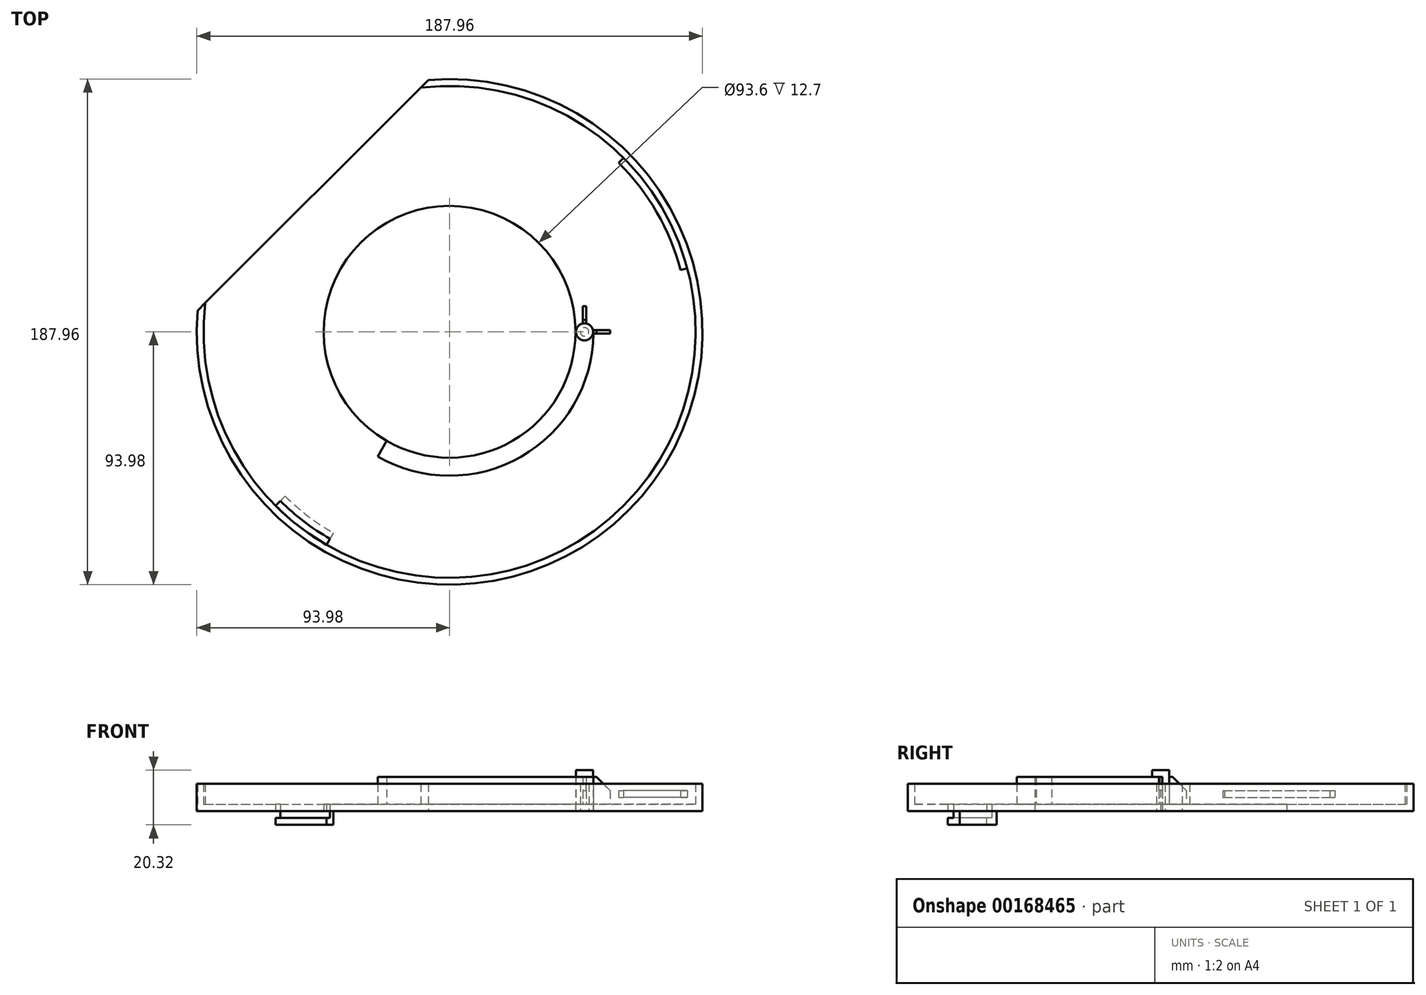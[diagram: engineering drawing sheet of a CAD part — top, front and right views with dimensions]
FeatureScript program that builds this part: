
annotation { "Feature Type Name" : "Feature", "Feature Type Description" : "" }
export const myFeature = defineFeature(function(context is Context, id is Id, definition is map)
    precondition{}
    {
        {
            var Q0;
            Q0=qCreatedBy(makeId("Top.planeOp"),FACE);
            var sketch = newSketch(context, id + "F0", { "sketchPlane" : qUnion([Q0])});
            skCircle(sketch, "E0", {"center": v(0, 0) * mm, "radius": 93.98 * mm});
            skCircle(sketch, "E1", {"center": v(0, 0) * mm, "radius": 46.8 * mm});
            skLineSegment(sketch, "E2", {"start": v(0, 92.98) * mm, "end": v(0, -89.42) * mm, "construction": true});
            skCircle(sketch, "E3", {"center": v(50.15, 0) * mm, "radius": 1.59 * mm});
            skCircle(sketch, "E4", {"center": v(50.15, 0) * mm, "radius": 3.18 * mm});
            skCircle(sketch, "E5", {"center": v(0, 0) * mm, "radius": 91.44 * mm});
            skLineSegment(sketch, "E6", {"start": v(0, 0) * mm, "end": v(-90.78, 24.32) * mm});
            skLineSegment(sketch, "E7", {"start": v(0, 0) * mm, "end": v(-66.45, 66.45) * mm});
            skCircle(sketch, "E8", {"center": v(0, 0) * mm, "radius": 88.9 * mm});
            skLineSegment(sketch, "E9.MirrorCS", {"start": v(0, 0) * mm, "end": v(66.45, 66.45) * mm});
            skLineSegment(sketch, "E10.MirrorCS", {"start": v(0, 0) * mm, "end": v(90.78, 24.32) * mm});
            skCircle(sketch, "E11", {"center": v(0, 0) * mm, "radius": 53.5 * mm});
            skPoint(sketch, "E12", {"position": v(46.8, 0) * mm});
            skPoint(sketch, "E13", {"position": v(53.5, 0) * mm});
            skLineSegment(sketch, "E14", {"start": v(46.8, 0) * mm, "end": v(53.5, 0) * mm});
            skLineSegment(sketch, "E15", {"start": v(0, 0) * mm, "end": v(103.4, 0) * mm, "construction": true});
            skLineSegment(sketch, "E16", {"start": v(49.52, 9.53) * mm, "end": v(49.52, -9.53) * mm});
            skLineSegment(sketch, "E17", {"start": v(50.78, 9.53) * mm, "end": v(50.78, -9.53) * mm});
            skLineSegment(sketch, "E18", {"start": v(50.78, -9.53) * mm, "end": v(49.52, -9.53) * mm});
            skLineSegment(sketch, "E19", {"start": v(50.78, 9.53) * mm, "end": v(49.52, 9.53) * mm});
            skPoint(sketch, "E20", {"position": v(49.52, 0) * mm});
            skLineSegment(sketch, "E21", {"start": v(50.15, 12) * mm, "end": v(50.15, -10.12) * mm, "construction": true});
            skPoint(sketch, "E22", {"position": v(50.15, 9.53) * mm});
            skLineSegment(sketch, "E23", {"start": v(50.15, 0.64) * mm, "end": v(59.67, 0.64) * mm});
            skLineSegment(sketch, "E24", {"start": v(59.67, -0.64) * mm, "end": v(59.67, 0.64) * mm});
            skLineSegment(sketch, "E25", {"start": v(50.15, -0.64) * mm, "end": v(59.67, -0.64) * mm});
            skPoint(sketch, "E26", {"position": v(59.67, 0) * mm});
            skLineSegment(sketch, "E27", {"start": v(0, 0) * mm, "end": v(-81.39, -47) * mm});
            skCircle(sketch, "E28", {"center": v(0, 0) * mm, "radius": 86.36 * mm});
            skLineSegment(sketch, "E29", {"start": v(0, 0) * mm, "end": v(-66.45, -66.45) * mm});
            skLineSegment(sketch, "E30", {"start": v(0, 0) * mm, "end": v(-46.99, -81.39) * mm});
            skLineSegment(sketch, "E31", {"start": v(-91.19, 6.77) * mm, "end": v(-6.77, 91.19) * mm});
            skLineSegment(sketch, "E32", {"start": v(-91.19, 6.77) * mm, "end": v(-93.9, 4.07) * mm});
            skLineSegment(sketch, "E33", {"start": v(-6.77, 91.19) * mm, "end": v(-4.07, 93.9) * mm});
            skLineSegment(sketch, "E34", {"start": v(-93.65, 7.9) * mm, "end": v(-7.9, 93.65) * mm});
            skSolve(sketch);
        }
        {
            var Q0;
            {var subQ0=sQuery(id+"F0.wireOp",EDGE,"E16");var subQ1=sQuery(id+"F0.wireOp",EDGE,"E3");var subQ2=makeQuery(id+"F0.imprint","INTERSECT",VERTEX,{"disambiguationData":[OD(0.0)],"derivedFrom":[subQ1,subQ0]});Q0=makeQuery(id+"F0.imprint","IMPRINT",FACE,{"disambiguationData":[TD([[makeQuery(id+"F0.imprint","IMPRINT",EDGE,{"disambiguationData":[TD([[subQ2,-1.0]])],"derivedFrom":subQ1}),-1.0]])]});}
            var Q1;
            {var subQ0=sQuery(id+"F0.wireOp",EDGE,"E25");var subQ1=sQuery(id+"F0.wireOp",EDGE,"E4");var subQ2=makeQuery(id+"F0.imprint","INTERSECT",VERTEX,{"derivedFrom":[subQ1,subQ0]});Q1=makeQuery(id+"F0.imprint","IMPRINT",FACE,{"disambiguationData":[TD([[makeQuery(id+"F0.imprint","IMPRINT",EDGE,{"disambiguationData":[TD([[subQ2,-1.0]])],"derivedFrom":subQ1}),-1.0]])]});}
            var Q2;
            {var subQ5=sQuery(id+"F0.wireOp",EDGE,"E11");var subQ6=sQuery(id+"F0.wireOp",EDGE,"E7");var subQ7=makeQuery(id+"F0.imprint","INTERSECT",VERTEX,{"derivedFrom":[subQ6,subQ5]});Q2=makeQuery(id+"F0.imprint","IMPRINT",FACE,{"disambiguationData":[TD([[makeQuery(id+"F0.imprint","IMPRINT",EDGE,{"disambiguationData":[TD([[subQ7,-1.0]])],"derivedFrom":subQ6}),-1.0]])]});}
            var Q3;
            {var subQ0=sQuery(id+"F0.wireOp",EDGE,"E17");var subQ1=sQuery(id+"F0.wireOp",EDGE,"E4");var subQ2=makeQuery(id+"F0.imprint","INTERSECT",VERTEX,{"disambiguationData":[OD(0.0)],"derivedFrom":[subQ1,subQ0]});Q3=makeQuery(id+"F0.imprint","IMPRINT",FACE,{"disambiguationData":[TD([[makeQuery(id+"F0.imprint","IMPRINT",EDGE,{"disambiguationData":[TD([[subQ2,1.0]])],"derivedFrom":subQ1}),1.0]])]});}
            var Q4;
            {var subQ0=sQuery(id+"F0.wireOp",EDGE,"E24");Q4=makeQuery(id+"F0.imprint","IMPRINT",FACE,{"disambiguationData":[TD([[makeQuery(id+"F0.imprint","IMPRINT",EDGE,{"derivedFrom":subQ0}),1.0]])]});}
            var Q5;
            {var subQ0=sQuery(id+"F0.wireOp",EDGE,"E17");var subQ1=sQuery(id+"F0.wireOp",EDGE,"E4");var subQ2=makeQuery(id+"F0.imprint","INTERSECT",VERTEX,{"disambiguationData":[OD(1.0)],"derivedFrom":[subQ1,subQ0]});Q5=makeQuery(id+"F0.imprint","IMPRINT",FACE,{"disambiguationData":[TD([[makeQuery(id+"F0.imprint","IMPRINT",EDGE,{"disambiguationData":[TD([[subQ2,-1.0]])],"derivedFrom":subQ1}),1.0]])]});}
            var Q6;
            {var subQ0=sQuery(id+"F0.wireOp",EDGE,"E9.MirrorCS");var subQ1=sQuery(id+"F0.wireOp",EDGE,"E0");var subQ2=makeQuery(id+"F0.imprint","INTERSECT",VERTEX,{"derivedFrom":[subQ1,subQ0]});Q6=makeQuery(id+"F0.imprint","IMPRINT",FACE,{"disambiguationData":[TD([[makeQuery(id+"F0.imprint","IMPRINT",EDGE,{"disambiguationData":[TD([[subQ2,1.0]])],"derivedFrom":subQ1}),1.0]])]});}
            var Q7;
            {var subQ0=sQuery(id+"F0.wireOp",EDGE,"E14");var subQ1=sQuery(id+"F0.wireOp",EDGE,"E4");var subQ2=makeQuery(id+"F0.imprint","INTERSECT",VERTEX,{"disambiguationData":[OD(1.0)],"derivedFrom":[subQ1,subQ0]});Q7=makeQuery(id+"F0.imprint","IMPRINT",FACE,{"disambiguationData":[TD([[makeQuery(id+"F0.imprint","IMPRINT",EDGE,{"disambiguationData":[TD([[subQ2,-1.0]])],"derivedFrom":subQ1}),-1.0]])]});}
            var Q8;
            {var subQ3=sQuery(id+"F0.wireOp",EDGE,"E9.MirrorCS");var subQ5=sQuery(id+"F0.wireOp",EDGE,"E8");var subQ6=makeQuery(id+"F0.imprint","INTERSECT",VERTEX,{"derivedFrom":[subQ5,subQ3]});Q8=makeQuery(id+"F0.imprint","IMPRINT",FACE,{"disambiguationData":[TD([[makeQuery(id+"F0.imprint","IMPRINT",EDGE,{"disambiguationData":[TD([[subQ6,-1.0]])],"derivedFrom":subQ5}),-1.0]])]});}
            var Q9;
            {var subQ0=sQuery(id+"F0.wireOp",EDGE,"E9.MirrorCS");var subQ1=sQuery(id+"F0.wireOp",EDGE,"E1");var subQ2=makeQuery(id+"F0.imprint","INTERSECT",VERTEX,{"derivedFrom":[subQ1,subQ0]});Q9=makeQuery(id+"F0.imprint","IMPRINT",FACE,{"disambiguationData":[TD([[makeQuery(id+"F0.imprint","IMPRINT",EDGE,{"disambiguationData":[TD([[subQ2,-1.0]])],"derivedFrom":subQ1}),-1.0]])]});}
            var Q10;
            {var subQ0=sQuery(id+"F0.wireOp",EDGE,"E10.MirrorCS");var subQ1=sQuery(id+"F0.wireOp",EDGE,"E1");var subQ2=makeQuery(id+"F0.imprint","INTERSECT",VERTEX,{"derivedFrom":[subQ1,subQ0]});Q10=makeQuery(id+"F0.imprint","IMPRINT",FACE,{"disambiguationData":[TD([[makeQuery(id+"F0.imprint","IMPRINT",EDGE,{"disambiguationData":[TD([[subQ2,-1.0]])],"derivedFrom":subQ1}),-1.0]])]});}
            var Q11;
            {var subQ5=sQuery(id+"F0.wireOp",EDGE,"E19");Q11=makeQuery(id+"F0.imprint","IMPRINT",FACE,{"disambiguationData":[TD([[makeQuery(id+"F0.imprint","IMPRINT",EDGE,{"derivedFrom":subQ5}),1.0]])]});}
            var Q12;
            {var subQ5=sQuery(id+"F0.wireOp",EDGE,"E11");var subQ7=sQuery(id+"F0.wireOp",EDGE,"E6");var subQ9=makeQuery(id+"F0.imprint","INTERSECT",VERTEX,{"derivedFrom":[subQ7,subQ5]});Q12=makeQuery(id+"F0.imprint","IMPRINT",FACE,{"disambiguationData":[TD([[makeQuery(id+"F0.imprint","IMPRINT",EDGE,{"disambiguationData":[TD([[subQ9,-1.0]])],"derivedFrom":subQ7}),1.0]])]});}
            var Q13;
            {var subQ0=sQuery(id+"F0.wireOp",EDGE,"E10.MirrorCS");var subQ1=sQuery(id+"F0.wireOp",EDGE,"E5");var subQ2=makeQuery(id+"F0.imprint","INTERSECT",VERTEX,{"derivedFrom":[subQ1,subQ0]});Q13=makeQuery(id+"F0.imprint","IMPRINT",FACE,{"disambiguationData":[TD([[makeQuery(id+"F0.imprint","IMPRINT",EDGE,{"disambiguationData":[TD([[subQ2,1.0]])],"derivedFrom":subQ1}),1.0]])]});}
            var Q14;
            {var subQ5=sQuery(id+"F0.wireOp",EDGE,"E18");Q14=makeQuery(id+"F0.imprint","IMPRINT",FACE,{"disambiguationData":[TD([[makeQuery(id+"F0.imprint","IMPRINT",EDGE,{"derivedFrom":subQ5}),-1.0]])]});}
            var Q15;
            {var subQ0=sQuery(id+"F0.wireOp",EDGE,"E11");var subQ1=sQuery(id+"F0.wireOp",EDGE,"E6");var subQ2=makeQuery(id+"F0.imprint","INTERSECT",VERTEX,{"derivedFrom":[subQ1,subQ0]});Q15=makeQuery(id+"F0.imprint","IMPRINT",FACE,{"disambiguationData":[TD([[makeQuery(id+"F0.imprint","IMPRINT",EDGE,{"disambiguationData":[TD([[subQ2,-1.0]])],"derivedFrom":subQ1}),-1.0]])]});}
            var Q16;
            {var subQ0=sQuery(id+"F0.wireOp",EDGE,"E16");var subQ1=sQuery(id+"F0.wireOp",EDGE,"E3");var subQ2=makeQuery(id+"F0.imprint","INTERSECT",VERTEX,{"disambiguationData":[OD(0.0)],"derivedFrom":[subQ1,subQ0]});Q16=makeQuery(id+"F0.imprint","IMPRINT",FACE,{"disambiguationData":[TD([[makeQuery(id+"F0.imprint","IMPRINT",EDGE,{"disambiguationData":[TD([[subQ2,-1.0]])],"derivedFrom":subQ1}),1.0]])]});}
            var Q17;
            {var subQ0=sQuery(id+"F0.wireOp",EDGE,"E14");var subQ1=sQuery(id+"F0.wireOp",EDGE,"E3");var subQ2=makeQuery(id+"F0.imprint","INTERSECT",VERTEX,{"disambiguationData":[OD(1.0)],"derivedFrom":[subQ1,subQ0]});Q17=makeQuery(id+"F0.imprint","IMPRINT",FACE,{"disambiguationData":[TD([[makeQuery(id+"F0.imprint","IMPRINT",EDGE,{"disambiguationData":[TD([[subQ2,-1.0]])],"derivedFrom":subQ1}),1.0]])]});}
            var Q18;
            {var subQ0=sQuery(id+"F0.wireOp",EDGE,"E17");var subQ1=sQuery(id+"F0.wireOp",EDGE,"E3");var subQ2=makeQuery(id+"F0.imprint","INTERSECT",VERTEX,{"disambiguationData":[OD(0.0)],"derivedFrom":[subQ1,subQ0]});Q18=makeQuery(id+"F0.imprint","IMPRINT",FACE,{"disambiguationData":[TD([[makeQuery(id+"F0.imprint","IMPRINT",EDGE,{"disambiguationData":[TD([[subQ2,-1.0]])],"derivedFrom":subQ1}),1.0]])]});}
            var Q19;
            {var subQ0=sQuery(id+"F0.wireOp",EDGE,"E14");var subQ1=sQuery(id+"F0.wireOp",EDGE,"E3");var subQ2=makeQuery(id+"F0.imprint","INTERSECT",VERTEX,{"disambiguationData":[OD(0.0)],"derivedFrom":[subQ1,subQ0]});Q19=makeQuery(id+"F0.imprint","IMPRINT",FACE,{"disambiguationData":[TD([[makeQuery(id+"F0.imprint","IMPRINT",EDGE,{"disambiguationData":[TD([[subQ2,-1.0]])],"derivedFrom":subQ1}),1.0]])]});}
            var Q20;
            {var subQ0=sQuery(id+"F0.wireOp",EDGE,"E6");var subQ1=sQuery(id+"F0.wireOp",EDGE,"E1");var subQ2=makeQuery(id+"F0.imprint","INTERSECT",VERTEX,{"derivedFrom":[subQ1,subQ0]});Q20=makeQuery(id+"F0.imprint","IMPRINT",FACE,{"disambiguationData":[TD([[makeQuery(id+"F0.imprint","IMPRINT",EDGE,{"disambiguationData":[TD([[subQ2,-1.0]])],"derivedFrom":subQ1}),-1.0]])]});}
            var Q21;
            {var subQ0=sQuery(id+"F0.wireOp",EDGE,"E25");var subQ1=sQuery(id+"F0.wireOp",EDGE,"E3");var subQ2=makeQuery(id+"F0.imprint","INTERSECT",VERTEX,{"derivedFrom":[subQ1,subQ0]});Q21=makeQuery(id+"F0.imprint","IMPRINT",FACE,{"disambiguationData":[TD([[makeQuery(id+"F0.imprint","IMPRINT",EDGE,{"disambiguationData":[TD([[subQ2,-1.0]])],"derivedFrom":subQ1}),-1.0]])]});}
            var Q22;
            {var subQ0=sQuery(id+"F0.wireOp",EDGE,"E7");var subQ1=sQuery(id+"F0.wireOp",EDGE,"E1");var subQ2=makeQuery(id+"F0.imprint","INTERSECT",VERTEX,{"derivedFrom":[subQ1,subQ0]});Q22=makeQuery(id+"F0.imprint","IMPRINT",FACE,{"disambiguationData":[TD([[makeQuery(id+"F0.imprint","IMPRINT",EDGE,{"disambiguationData":[TD([[subQ2,-1.0]])],"derivedFrom":subQ1}),-1.0]])]});}
            var Q23;
            {var subQ0=sQuery(id+"F0.wireOp",EDGE,"E9.MirrorCS");var subQ1=sQuery(id+"F0.wireOp",EDGE,"E5");var subQ2=makeQuery(id+"F0.imprint","INTERSECT",VERTEX,{"derivedFrom":[subQ1,subQ0]});Q23=makeQuery(id+"F0.imprint","IMPRINT",FACE,{"disambiguationData":[TD([[makeQuery(id+"F0.imprint","IMPRINT",EDGE,{"disambiguationData":[TD([[subQ2,1.0]])],"derivedFrom":subQ1}),1.0]])]});}
            var Q24;
            {var subQ0=sQuery(id+"F0.wireOp",EDGE,"E14");var subQ1=sQuery(id+"F0.wireOp",EDGE,"E3");var subQ2=makeQuery(id+"F0.imprint","INTERSECT",VERTEX,{"disambiguationData":[OD(0.0)],"derivedFrom":[subQ1,subQ0]});Q24=makeQuery(id+"F0.imprint","IMPRINT",FACE,{"disambiguationData":[TD([[makeQuery(id+"F0.imprint","IMPRINT",EDGE,{"disambiguationData":[TD([[subQ2,-1.0]])],"derivedFrom":subQ1}),-1.0]])]});}
            var Q25;
            {var subQ16=sQuery(id+"F0.wireOp",EDGE,"E19");Q25=makeQuery(id+"F0.imprint","IMPRINT",FACE,{"disambiguationData":[TD([[makeQuery(id+"F0.imprint","IMPRINT",EDGE,{"derivedFrom":subQ16}),-1.0]])]});}
            var Q26;
            {var subQ13=sQuery(id+"F0.wireOp",EDGE,"E18");Q26=makeQuery(id+"F0.imprint","IMPRINT",FACE,{"disambiguationData":[TD([[makeQuery(id+"F0.imprint","IMPRINT",EDGE,{"derivedFrom":subQ13}),1.0]])]});}
            var Q27;
            {var subQ0=sQuery(id+"F0.wireOp",EDGE,"E24");Q27=makeQuery(id+"F0.imprint","IMPRINT",FACE,{"disambiguationData":[TD([[makeQuery(id+"F0.imprint","IMPRINT",EDGE,{"derivedFrom":subQ0}),-1.0]])]});}
            var Q28;
            {var subQ0=sQuery(id+"F0.wireOp",EDGE,"E9.MirrorCS");var subQ1=sQuery(id+"F0.wireOp",EDGE,"E8");var subQ2=makeQuery(id+"F0.imprint","INTERSECT",VERTEX,{"derivedFrom":[subQ1,subQ0]});Q28=makeQuery(id+"F0.imprint","IMPRINT",FACE,{"disambiguationData":[TD([[makeQuery(id+"F0.imprint","IMPRINT",EDGE,{"disambiguationData":[TD([[subQ2,1.0]])],"derivedFrom":subQ1}),1.0]])]});}
            var Q29;
            {var subQ1=sQuery(id+"F0.wireOp",EDGE,"E3");var subQ5=sQuery(id+"F0.wireOp",EDGE,"E14");var subQ6=makeQuery(id+"F0.imprint","INTERSECT",VERTEX,{"disambiguationData":[OD(1.0)],"derivedFrom":[subQ1,subQ5]});Q29=makeQuery(id+"F0.imprint","IMPRINT",FACE,{"disambiguationData":[TD([[makeQuery(id+"F0.imprint","IMPRINT",EDGE,{"disambiguationData":[TD([[subQ6,-1.0]])],"derivedFrom":subQ1}),-1.0]])]});}
            var Q30;
            {var subQ3=sQuery(id+"F0.wireOp",EDGE,"E25");var subQ6=sQuery(id+"F0.wireOp",EDGE,"E3");var subQ9=makeQuery(id+"F0.imprint","INTERSECT",VERTEX,{"derivedFrom":[subQ6,subQ3]});Q30=makeQuery(id+"F0.imprint","IMPRINT",FACE,{"disambiguationData":[TD([[makeQuery(id+"F0.imprint","IMPRINT",EDGE,{"disambiguationData":[TD([[subQ9,1.0]])],"derivedFrom":subQ6}),-1.0]])]});}
            var Q31;
            {var subQ1=sQuery(id+"F0.wireOp",EDGE,"E3");var subQ5=sQuery(id+"F0.wireOp",EDGE,"E17");var subQ6=makeQuery(id+"F0.imprint","INTERSECT",VERTEX,{"disambiguationData":[OD(0.0)],"derivedFrom":[subQ1,subQ5]});Q31=makeQuery(id+"F0.imprint","IMPRINT",FACE,{"disambiguationData":[TD([[makeQuery(id+"F0.imprint","IMPRINT",EDGE,{"disambiguationData":[TD([[subQ6,-1.0]])],"derivedFrom":subQ1}),-1.0]])]});}
            var Q32;
            {var subQ5=sQuery(id+"F0.wireOp",EDGE,"E3");var subQ6=makeQuery(id+"F0.imprint","INTERSECT",VERTEX,{"derivedFrom":[subQ5,sQuery(id+"F0.wireOp",EDGE,"E25")]});Q32=makeQuery(id+"F0.imprint","IMPRINT",FACE,{"disambiguationData":[TD([[makeQuery(id+"F0.imprint","IMPRINT",EDGE,{"disambiguationData":[TD([[subQ6,1.0]])],"derivedFrom":subQ5}),1.0]])]});}
            var Q33;
            {var subQ1=sQuery(id+"F0.wireOp",EDGE,"E3");var subQ7=makeQuery(id+"F0.imprint","INTERSECT",VERTEX,{"derivedFrom":[subQ1,sQuery(id+"F0.wireOp",EDGE,"E23")]});Q33=makeQuery(id+"F0.imprint","IMPRINT",FACE,{"disambiguationData":[TD([[makeQuery(id+"F0.imprint","IMPRINT",EDGE,{"disambiguationData":[TD([[subQ7,-1.0]])],"derivedFrom":subQ1}),1.0]])]});}
            var Q34;
            {var subQ1=sQuery(id+"F0.wireOp",EDGE,"E3");var subQ7=sQuery(id+"F0.wireOp",EDGE,"E23");var subQ9=makeQuery(id+"F0.imprint","INTERSECT",VERTEX,{"derivedFrom":[subQ1,subQ7]});Q34=makeQuery(id+"F0.imprint","IMPRINT",FACE,{"disambiguationData":[TD([[makeQuery(id+"F0.imprint","IMPRINT",EDGE,{"disambiguationData":[TD([[subQ9,-1.0]])],"derivedFrom":subQ1}),-1.0]])]});}
            var Q35;
            {var subQ0=sQuery(id+"F0.wireOp",EDGE,"E23");var subQ1=sQuery(id+"F0.wireOp",EDGE,"E3");var subQ2=makeQuery(id+"F0.imprint","INTERSECT",VERTEX,{"derivedFrom":[subQ1,subQ0]});Q35=makeQuery(id+"F0.imprint","IMPRINT",FACE,{"disambiguationData":[TD([[makeQuery(id+"F0.imprint","IMPRINT",EDGE,{"disambiguationData":[TD([[subQ2,1.0]])],"derivedFrom":subQ1}),-1.0]])]});}
            var Q36;
            {var subQ0=sQuery(id+"F0.wireOp",EDGE,"E10.MirrorCS");var subQ1=sQuery(id+"F0.wireOp",EDGE,"E0");var subQ2=makeQuery(id+"F0.imprint","INTERSECT",VERTEX,{"derivedFrom":[subQ1,subQ0]});Q36=makeQuery(id+"F0.imprint","IMPRINT",FACE,{"disambiguationData":[TD([[makeQuery(id+"F0.imprint","IMPRINT",EDGE,{"disambiguationData":[TD([[subQ2,1.0]])],"derivedFrom":subQ1}),1.0]])]});}
            var Q37;
            {var subQ0=sQuery(id+"F0.wireOp",EDGE,"E27");var subQ1=sQuery(id+"F0.wireOp",EDGE,"E1");var subQ2=makeQuery(id+"F0.imprint","INTERSECT",VERTEX,{"derivedFrom":[subQ1,subQ0]});Q37=makeQuery(id+"F0.imprint","IMPRINT",FACE,{"disambiguationData":[TD([[makeQuery(id+"F0.imprint","IMPRINT",EDGE,{"disambiguationData":[TD([[subQ2,-1.0]])],"derivedFrom":subQ1}),-1.0]])]});}
            var Q38;
            {var subQ0=sQuery(id+"F0.wireOp",EDGE,"E27");var subQ1=sQuery(id+"F0.wireOp",EDGE,"E11");var subQ2=makeQuery(id+"F0.imprint","INTERSECT",VERTEX,{"derivedFrom":[subQ1,subQ0]});Q38=makeQuery(id+"F0.imprint","IMPRINT",FACE,{"disambiguationData":[TD([[makeQuery(id+"F0.imprint","IMPRINT",EDGE,{"disambiguationData":[TD([[subQ2,-1.0]])],"derivedFrom":subQ1}),-1.0]])]});}
            var Q39;
            {var subQ0=sQuery(id+"F0.wireOp",EDGE,"E27");var subQ1=sQuery(id+"F0.wireOp",EDGE,"E8");var subQ2=makeQuery(id+"F0.imprint","INTERSECT",VERTEX,{"derivedFrom":[subQ1,subQ0]});Q39=makeQuery(id+"F0.imprint","IMPRINT",FACE,{"disambiguationData":[TD([[makeQuery(id+"F0.imprint","IMPRINT",EDGE,{"disambiguationData":[TD([[subQ2,-1.0]])],"derivedFrom":subQ1}),1.0]])]});}
            var Q40;
            {var subQ0=sQuery(id+"F0.wireOp",EDGE,"E29");var subQ1=sQuery(id+"F0.wireOp",EDGE,"E1");var subQ2=makeQuery(id+"F0.imprint","INTERSECT",VERTEX,{"derivedFrom":[subQ1,subQ0]});Q40=makeQuery(id+"F0.imprint","IMPRINT",FACE,{"disambiguationData":[TD([[makeQuery(id+"F0.imprint","IMPRINT",EDGE,{"disambiguationData":[TD([[subQ2,-1.0]])],"derivedFrom":subQ1}),-1.0]])]});}
            var Q41;
            {var subQ0=sQuery(id+"F0.wireOp",EDGE,"E29");var subQ1=sQuery(id+"F0.wireOp",EDGE,"E8");var subQ2=makeQuery(id+"F0.imprint","INTERSECT",VERTEX,{"derivedFrom":[subQ1,subQ0]});Q41=makeQuery(id+"F0.imprint","IMPRINT",FACE,{"disambiguationData":[TD([[makeQuery(id+"F0.imprint","IMPRINT",EDGE,{"disambiguationData":[TD([[subQ2,-1.0]])],"derivedFrom":subQ1}),1.0]])]});}
            var Q42;
            {var subQ0=sQuery(id+"F0.wireOp",EDGE,"E10.MirrorCS");var subQ1=sQuery(id+"F0.wireOp",EDGE,"E8");var subQ2=makeQuery(id+"F0.imprint","INTERSECT",VERTEX,{"derivedFrom":[subQ1,subQ0]});Q42=makeQuery(id+"F0.imprint","IMPRINT",FACE,{"disambiguationData":[TD([[makeQuery(id+"F0.imprint","IMPRINT",EDGE,{"disambiguationData":[TD([[subQ2,1.0]])],"derivedFrom":subQ1}),1.0]])]});}
            var Q43;
            {var subQ0=sQuery(id+"F0.wireOp",EDGE,"E11");var subQ1=sQuery(id+"F0.wireOp",EDGE,"E9.MirrorCS");var subQ2=makeQuery(id+"F0.imprint","INTERSECT",VERTEX,{"derivedFrom":[subQ1,subQ0]});Q43=makeQuery(id+"F0.imprint","IMPRINT",FACE,{"disambiguationData":[TD([[makeQuery(id+"F0.imprint","IMPRINT",EDGE,{"disambiguationData":[TD([[subQ2,-1.0]])],"derivedFrom":subQ1}),-1.0]])]});}
            var Q44;
            {var subQ0=sQuery(id+"F0.wireOp",EDGE,"E29");var subQ1=sQuery(id+"F0.wireOp",EDGE,"E11");var subQ2=makeQuery(id+"F0.imprint","INTERSECT",VERTEX,{"derivedFrom":[subQ1,subQ0]});Q44=makeQuery(id+"F0.imprint","IMPRINT",FACE,{"disambiguationData":[TD([[makeQuery(id+"F0.imprint","IMPRINT",EDGE,{"disambiguationData":[TD([[subQ2,-1.0]])],"derivedFrom":subQ1}),-1.0]])]});}
            var Q45;
            {var subQ0=sQuery(id+"F0.wireOp",EDGE,"E27");var subQ1=sQuery(id+"F0.wireOp",EDGE,"E0");var subQ2=makeQuery(id+"F0.imprint","INTERSECT",VERTEX,{"derivedFrom":[subQ1,subQ0]});Q45=makeQuery(id+"F0.imprint","IMPRINT",FACE,{"disambiguationData":[TD([[makeQuery(id+"F0.imprint","IMPRINT",EDGE,{"disambiguationData":[TD([[subQ2,-1.0]])],"derivedFrom":subQ1}),1.0]])]});}
            var Q46;
            {var subQ0=sQuery(id+"F0.wireOp",EDGE,"E29");var subQ1=sQuery(id+"F0.wireOp",EDGE,"E0");var subQ2=makeQuery(id+"F0.imprint","INTERSECT",VERTEX,{"derivedFrom":[subQ1,subQ0]});Q46=makeQuery(id+"F0.imprint","IMPRINT",FACE,{"disambiguationData":[TD([[makeQuery(id+"F0.imprint","IMPRINT",EDGE,{"disambiguationData":[TD([[subQ2,-1.0]])],"derivedFrom":subQ1}),1.0]])]});}
            var Q47;
            {var subQ0=sQuery(id+"F0.wireOp",EDGE,"E27");var subQ1=sQuery(id+"F0.wireOp",EDGE,"E5");var subQ2=makeQuery(id+"F0.imprint","INTERSECT",VERTEX,{"derivedFrom":[subQ1,subQ0]});Q47=makeQuery(id+"F0.imprint","IMPRINT",FACE,{"disambiguationData":[TD([[makeQuery(id+"F0.imprint","IMPRINT",EDGE,{"disambiguationData":[TD([[subQ2,-1.0]])],"derivedFrom":subQ1}),1.0]])]});}
            var Q48;
            {var subQ0=sQuery(id+"F0.wireOp",EDGE,"E29");var subQ1=sQuery(id+"F0.wireOp",EDGE,"E5");var subQ2=makeQuery(id+"F0.imprint","INTERSECT",VERTEX,{"derivedFrom":[subQ1,subQ0]});Q48=makeQuery(id+"F0.imprint","IMPRINT",FACE,{"disambiguationData":[TD([[makeQuery(id+"F0.imprint","IMPRINT",EDGE,{"disambiguationData":[TD([[subQ2,-1.0]])],"derivedFrom":subQ1}),1.0]])]});}
            var Q49;
            {var subQ0=sQuery(id+"F0.wireOp",EDGE,"E9.MirrorCS");var subQ1=sQuery(id+"F0.wireOp",EDGE,"E8");var subQ2=makeQuery(id+"F0.imprint","INTERSECT",VERTEX,{"derivedFrom":[subQ1,subQ0]});Q49=makeQuery(id+"F0.imprint","IMPRINT",FACE,{"disambiguationData":[TD([[makeQuery(id+"F0.imprint","IMPRINT",EDGE,{"disambiguationData":[TD([[subQ2,-1.0]])],"derivedFrom":subQ1}),1.0]])]});}
            var Q50;
            {var subQ3=sQuery(id+"F0.wireOp",EDGE,"E32");Q50=makeQuery(id+"F0.imprint","IMPRINT",FACE,{"disambiguationData":[TD([[makeQuery(id+"F0.imprint","IMPRINT",EDGE,{"derivedFrom":subQ3}),1.0]])]});}
            var Q51;
            {var subQ0=sQuery(id+"F0.wireOp",EDGE,"E31");var subQ5=sQuery(id+"F0.wireOp",EDGE,"E8");var subQ6=makeQuery(id+"F0.imprint","INTERSECT",VERTEX,{"disambiguationData":[OD(1.0)],"derivedFrom":[subQ5,subQ0]});Q51=makeQuery(id+"F0.imprint","IMPRINT",FACE,{"disambiguationData":[TD([[makeQuery(id+"F0.imprint","IMPRINT",EDGE,{"disambiguationData":[TD([[subQ6,-1.0]])],"derivedFrom":subQ5}),-1.0]])]});}
            var Q52;
            {var subQ0=sQuery(id+"F0.wireOp",EDGE,"E31");var subQ1=sQuery(id+"F0.wireOp",EDGE,"E8");var subQ2=makeQuery(id+"F0.imprint","INTERSECT",VERTEX,{"disambiguationData":[OD(1.0)],"derivedFrom":[subQ1,subQ0]});Q52=makeQuery(id+"F0.imprint","IMPRINT",FACE,{"disambiguationData":[TD([[makeQuery(id+"F0.imprint","IMPRINT",EDGE,{"disambiguationData":[TD([[subQ2,-1.0]])],"derivedFrom":subQ1}),1.0]])]});}
            var Q53;
            {var subQ3=sQuery(id+"F0.wireOp",EDGE,"E33");Q53=makeQuery(id+"F0.imprint","IMPRINT",FACE,{"disambiguationData":[TD([[makeQuery(id+"F0.imprint","IMPRINT",EDGE,{"derivedFrom":subQ3}),-1.0]])]});}
            var Q54;
            {var subQ0=sQuery(id+"F0.wireOp",EDGE,"E32");Q54=makeQuery(id+"F0.imprint","IMPRINT",FACE,{"disambiguationData":[TD([[makeQuery(id+"F0.imprint","IMPRINT",EDGE,{"derivedFrom":subQ0}),-1.0]])]});}
            var Q55;
            {var subQ3=sQuery(id+"F0.wireOp",EDGE,"E34");var subQ5=sQuery(id+"F0.wireOp",EDGE,"E8");var subQ7=makeQuery(id+"F0.imprint","INTERSECT",VERTEX,{"disambiguationData":[OD(1.0)],"derivedFrom":[subQ5,subQ3]});Q55=makeQuery(id+"F0.imprint","IMPRINT",FACE,{"disambiguationData":[TD([[makeQuery(id+"F0.imprint","IMPRINT",EDGE,{"disambiguationData":[TD([[subQ7,-1.0]])],"derivedFrom":subQ5}),-1.0]])]});}
            var Q56;
            {var subQ0=sQuery(id+"F0.wireOp",EDGE,"E34");var subQ1=sQuery(id+"F0.wireOp",EDGE,"E8");var subQ2=makeQuery(id+"F0.imprint","INTERSECT",VERTEX,{"disambiguationData":[OD(1.0)],"derivedFrom":[subQ1,subQ0]});Q56=makeQuery(id+"F0.imprint","IMPRINT",FACE,{"disambiguationData":[TD([[makeQuery(id+"F0.imprint","IMPRINT",EDGE,{"disambiguationData":[TD([[subQ2,-1.0]])],"derivedFrom":subQ1}),1.0]])]});}
            var Q57;
            {var subQ0=sQuery(id+"F0.wireOp",EDGE,"E31");var subQ1=sQuery(id+"F0.wireOp",EDGE,"E6");var subQ2=makeQuery(id+"F0.imprint","INTERSECT",VERTEX,{"derivedFrom":[subQ1,subQ0]});Q57=makeQuery(id+"F0.imprint","IMPRINT",FACE,{"disambiguationData":[TD([[makeQuery(id+"F0.imprint","IMPRINT",EDGE,{"disambiguationData":[TD([[subQ2,-1.0]])],"derivedFrom":subQ1}),1.0]])]});}
            var Q58;
            {var subQ0=sQuery(id+"F0.wireOp",EDGE,"E31");var subQ1=sQuery(id+"F0.wireOp",EDGE,"E6");var subQ2=makeQuery(id+"F0.imprint","INTERSECT",VERTEX,{"derivedFrom":[subQ1,subQ0]});Q58=makeQuery(id+"F0.imprint","IMPRINT",FACE,{"disambiguationData":[TD([[makeQuery(id+"F0.imprint","IMPRINT",EDGE,{"disambiguationData":[TD([[subQ2,-1.0]])],"derivedFrom":subQ1}),-1.0]])]});}
            var Q59;
            {var subQ0=sQuery(id+"F0.wireOp",EDGE,"E31");var subQ1=sQuery(id+"F0.wireOp",EDGE,"E7");var subQ2=makeQuery(id+"F0.imprint","INTERSECT",VERTEX,{"derivedFrom":[subQ1,subQ0]});Q59=makeQuery(id+"F0.imprint","IMPRINT",FACE,{"disambiguationData":[TD([[makeQuery(id+"F0.imprint","IMPRINT",EDGE,{"disambiguationData":[TD([[subQ2,-1.0]])],"derivedFrom":subQ1}),-1.0]])]});}
            var Q60;
            {var subQ0=sQuery(id+"F0.wireOp",EDGE,"E31");var subQ1=sQuery(id+"F0.wireOp",EDGE,"E8");var subQ2=makeQuery(id+"F0.imprint","INTERSECT",VERTEX,{"disambiguationData":[OD(0.0)],"derivedFrom":[subQ1,subQ0]});Q60=makeQuery(id+"F0.imprint","IMPRINT",FACE,{"disambiguationData":[TD([[makeQuery(id+"F0.imprint","IMPRINT",EDGE,{"disambiguationData":[TD([[subQ2,-1.0]])],"derivedFrom":subQ1}),1.0]])]});}
            var Q61;
            {var subQ0=sQuery(id+"F0.wireOp",EDGE,"E31");var subQ5=sQuery(id+"F0.wireOp",EDGE,"E8");var subQ6=makeQuery(id+"F0.imprint","INTERSECT",VERTEX,{"disambiguationData":[OD(0.0)],"derivedFrom":[subQ5,subQ0]});Q61=makeQuery(id+"F0.imprint","IMPRINT",FACE,{"disambiguationData":[TD([[makeQuery(id+"F0.imprint","IMPRINT",EDGE,{"disambiguationData":[TD([[subQ6,-1.0]])],"derivedFrom":subQ5}),-1.0]])]});}
            var Q62;
            {var subQ0=sQuery(id+"F0.wireOp",EDGE,"E33");Q62=makeQuery(id+"F0.imprint","IMPRINT",FACE,{"disambiguationData":[TD([[makeQuery(id+"F0.imprint","IMPRINT",EDGE,{"derivedFrom":subQ0}),1.0]])]});}
            extrude(context, id + "F1", {"entities" : qUnion([Q0, Q1, Q2, Q3, Q4, Q5, Q6, Q7, Q8, Q9, Q10, Q11, Q12, Q13, Q14, Q15, Q16, Q17, Q18, Q19, Q20, Q21, Q22, Q23, Q24, Q25, Q26, Q27, Q28, Q29, Q30, Q31, Q32, Q33, Q34, Q35, Q36, Q37, Q38, Q39, Q40, Q41, Q42, Q43, Q44, Q45, Q46, Q47, Q48, Q49, Q50, Q51, Q52, Q53, Q54, Q55, Q56, Q57, Q58, Q59, Q60, Q61, Q62]), "depth" : 2.54 * mm});
        }
        {
            var Q0;
            {var subQ0=sQuery(id+"F0.wireOp",EDGE,"E25");var subQ1=sQuery(id+"F0.wireOp",EDGE,"E3");var subQ2=makeQuery(id+"F0.imprint","INTERSECT",VERTEX,{"derivedFrom":[subQ1,subQ0]});Q0=makeQuery(id+"F0.imprint","IMPRINT",FACE,{"disambiguationData":[TD([[makeQuery(id+"F0.imprint","IMPRINT",EDGE,{"disambiguationData":[TD([[subQ2,-1.0]])],"derivedFrom":subQ1}),-1.0]])]});}
            var Q1;
            {var subQ0=sQuery(id+"F0.wireOp",EDGE,"E23");var subQ1=sQuery(id+"F0.wireOp",EDGE,"E3");var subQ2=makeQuery(id+"F0.imprint","INTERSECT",VERTEX,{"derivedFrom":[subQ1,subQ0]});Q1=makeQuery(id+"F0.imprint","IMPRINT",FACE,{"disambiguationData":[TD([[makeQuery(id+"F0.imprint","IMPRINT",EDGE,{"disambiguationData":[TD([[subQ2,1.0]])],"derivedFrom":subQ1}),-1.0]])]});}
            var Q2;
            {var subQ5=sQuery(id+"F0.wireOp",EDGE,"E3");var subQ7=makeQuery(id+"F0.imprint","INTERSECT",VERTEX,{"derivedFrom":[subQ5,sQuery(id+"F0.wireOp",EDGE,"E23")]});Q2=makeQuery(id+"F0.imprint","IMPRINT",FACE,{"disambiguationData":[TD([[makeQuery(id+"F0.imprint","IMPRINT",EDGE,{"disambiguationData":[TD([[subQ7,-1.0]])],"derivedFrom":subQ5}),1.0]])]});}
            var Q3;
            {var subQ1=sQuery(id+"F0.wireOp",EDGE,"E3");var subQ7=makeQuery(id+"F0.imprint","INTERSECT",VERTEX,{"derivedFrom":[subQ1,sQuery(id+"F0.wireOp",EDGE,"E25")]});Q3=makeQuery(id+"F0.imprint","IMPRINT",FACE,{"disambiguationData":[TD([[makeQuery(id+"F0.imprint","IMPRINT",EDGE,{"disambiguationData":[TD([[subQ7,1.0]])],"derivedFrom":subQ1}),1.0]])]});}
            var Q4;
            {var subQ3=sQuery(id+"F0.wireOp",EDGE,"E25");var subQ6=sQuery(id+"F0.wireOp",EDGE,"E3");var subQ9=makeQuery(id+"F0.imprint","INTERSECT",VERTEX,{"derivedFrom":[subQ6,subQ3]});Q4=makeQuery(id+"F0.imprint","IMPRINT",FACE,{"disambiguationData":[TD([[makeQuery(id+"F0.imprint","IMPRINT",EDGE,{"disambiguationData":[TD([[subQ9,1.0]])],"derivedFrom":subQ6}),-1.0]])]});}
            var Q5;
            {var subQ0=sQuery(id+"F0.wireOp",EDGE,"E17");var subQ1=sQuery(id+"F0.wireOp",EDGE,"E3");var subQ2=makeQuery(id+"F0.imprint","INTERSECT",VERTEX,{"disambiguationData":[OD(0.0)],"derivedFrom":[subQ1,subQ0]});Q5=makeQuery(id+"F0.imprint","IMPRINT",FACE,{"disambiguationData":[TD([[makeQuery(id+"F0.imprint","IMPRINT",EDGE,{"disambiguationData":[TD([[subQ2,-1.0]])],"derivedFrom":subQ1}),-1.0]])]});}
            var Q6;
            {var subQ0=sQuery(id+"F0.wireOp",EDGE,"E14");var subQ1=sQuery(id+"F0.wireOp",EDGE,"E3");var subQ2=makeQuery(id+"F0.imprint","INTERSECT",VERTEX,{"disambiguationData":[OD(1.0)],"derivedFrom":[subQ1,subQ0]});Q6=makeQuery(id+"F0.imprint","IMPRINT",FACE,{"disambiguationData":[TD([[makeQuery(id+"F0.imprint","IMPRINT",EDGE,{"disambiguationData":[TD([[subQ2,-1.0]])],"derivedFrom":subQ1}),-1.0]])]});}
            var Q7;
            {var subQ0=sQuery(id+"F0.wireOp",EDGE,"E16");var subQ1=sQuery(id+"F0.wireOp",EDGE,"E3");var subQ2=makeQuery(id+"F0.imprint","INTERSECT",VERTEX,{"disambiguationData":[OD(0.0)],"derivedFrom":[subQ1,subQ0]});Q7=makeQuery(id+"F0.imprint","IMPRINT",FACE,{"disambiguationData":[TD([[makeQuery(id+"F0.imprint","IMPRINT",EDGE,{"disambiguationData":[TD([[subQ2,-1.0]])],"derivedFrom":subQ1}),-1.0]])]});}
            var Q8;
            {var subQ0=sQuery(id+"F0.wireOp",EDGE,"E17");var subQ1=sQuery(id+"F0.wireOp",EDGE,"E4");var subQ2=makeQuery(id+"F0.imprint","INTERSECT",VERTEX,{"disambiguationData":[OD(1.0)],"derivedFrom":[subQ1,subQ0]});Q8=makeQuery(id+"F0.imprint","IMPRINT",FACE,{"disambiguationData":[TD([[makeQuery(id+"F0.imprint","IMPRINT",EDGE,{"disambiguationData":[TD([[subQ2,-1.0]])],"derivedFrom":subQ1}),1.0]])]});}
            var Q9;
            {var subQ0=sQuery(id+"F0.wireOp",EDGE,"E14");var subQ1=sQuery(id+"F0.wireOp",EDGE,"E3");var subQ2=makeQuery(id+"F0.imprint","INTERSECT",VERTEX,{"disambiguationData":[OD(1.0)],"derivedFrom":[subQ1,subQ0]});Q9=makeQuery(id+"F0.imprint","IMPRINT",FACE,{"disambiguationData":[TD([[makeQuery(id+"F0.imprint","IMPRINT",EDGE,{"disambiguationData":[TD([[subQ2,-1.0]])],"derivedFrom":subQ1}),1.0]])]});}
            var Q10;
            {var subQ0=sQuery(id+"F0.wireOp",EDGE,"E17");var subQ1=sQuery(id+"F0.wireOp",EDGE,"E4");var subQ2=makeQuery(id+"F0.imprint","INTERSECT",VERTEX,{"disambiguationData":[OD(0.0)],"derivedFrom":[subQ1,subQ0]});Q10=makeQuery(id+"F0.imprint","IMPRINT",FACE,{"disambiguationData":[TD([[makeQuery(id+"F0.imprint","IMPRINT",EDGE,{"disambiguationData":[TD([[subQ2,1.0]])],"derivedFrom":subQ1}),1.0]])]});}
            var Q11;
            {var subQ0=sQuery(id+"F0.wireOp",EDGE,"E16");var subQ1=sQuery(id+"F0.wireOp",EDGE,"E3");var subQ2=makeQuery(id+"F0.imprint","INTERSECT",VERTEX,{"disambiguationData":[OD(0.0)],"derivedFrom":[subQ1,subQ0]});Q11=makeQuery(id+"F0.imprint","IMPRINT",FACE,{"disambiguationData":[TD([[makeQuery(id+"F0.imprint","IMPRINT",EDGE,{"disambiguationData":[TD([[subQ2,-1.0]])],"derivedFrom":subQ1}),1.0]])]});}
            var Q12;
            {var subQ0=sQuery(id+"F0.wireOp",EDGE,"E14");var subQ1=sQuery(id+"F0.wireOp",EDGE,"E3");var subQ2=makeQuery(id+"F0.imprint","INTERSECT",VERTEX,{"disambiguationData":[OD(0.0)],"derivedFrom":[subQ1,subQ0]});Q12=makeQuery(id+"F0.imprint","IMPRINT",FACE,{"disambiguationData":[TD([[makeQuery(id+"F0.imprint","IMPRINT",EDGE,{"disambiguationData":[TD([[subQ2,-1.0]])],"derivedFrom":subQ1}),1.0]])]});}
            var Q13;
            {var subQ0=sQuery(id+"F0.wireOp",EDGE,"E17");var subQ1=sQuery(id+"F0.wireOp",EDGE,"E3");var subQ2=makeQuery(id+"F0.imprint","INTERSECT",VERTEX,{"disambiguationData":[OD(0.0)],"derivedFrom":[subQ1,subQ0]});Q13=makeQuery(id+"F0.imprint","IMPRINT",FACE,{"disambiguationData":[TD([[makeQuery(id+"F0.imprint","IMPRINT",EDGE,{"disambiguationData":[TD([[subQ2,-1.0]])],"derivedFrom":subQ1}),1.0]])]});}
            var Q14;
            {var subQ0=sQuery(id+"F0.wireOp",EDGE,"E14");var subQ1=sQuery(id+"F0.wireOp",EDGE,"E3");var subQ2=makeQuery(id+"F0.imprint","INTERSECT",VERTEX,{"disambiguationData":[OD(0.0)],"derivedFrom":[subQ1,subQ0]});Q14=makeQuery(id+"F0.imprint","IMPRINT",FACE,{"disambiguationData":[TD([[makeQuery(id+"F0.imprint","IMPRINT",EDGE,{"disambiguationData":[TD([[subQ2,-1.0]])],"derivedFrom":subQ1}),-1.0]])]});}
            var Q15;
            {var subQ3=sQuery(id+"F0.wireOp",EDGE,"E23");var subQ6=sQuery(id+"F0.wireOp",EDGE,"E3");var subQ9=makeQuery(id+"F0.imprint","INTERSECT",VERTEX,{"derivedFrom":[subQ6,subQ3]});Q15=makeQuery(id+"F0.imprint","IMPRINT",FACE,{"disambiguationData":[TD([[makeQuery(id+"F0.imprint","IMPRINT",EDGE,{"disambiguationData":[TD([[subQ9,-1.0]])],"derivedFrom":subQ6}),-1.0]])]});}
            var Q16;
            {var subQ0=sQuery(id+"F0.wireOp",EDGE,"E16");var subQ1=sQuery(id+"F0.wireOp",EDGE,"E3");var subQ2=makeQuery(id+"F0.imprint","INTERSECT",VERTEX,{"disambiguationData":[OD(1.0)],"derivedFrom":[subQ1,subQ0]});Q16=makeQuery(id+"F0.imprint","IMPRINT",FACE,{"disambiguationData":[TD([[makeQuery(id+"F0.imprint","IMPRINT",EDGE,{"disambiguationData":[TD([[subQ2,-1.0]])],"derivedFrom":subQ1}),-1.0]])]});}
            var Q17;
            {var subQ0=sQuery(id+"F0.wireOp",EDGE,"E16");var subQ1=sQuery(id+"F0.wireOp",EDGE,"E3");var subQ2=makeQuery(id+"F0.imprint","INTERSECT",VERTEX,{"disambiguationData":[OD(1.0)],"derivedFrom":[subQ1,subQ0]});Q17=makeQuery(id+"F0.imprint","IMPRINT",FACE,{"disambiguationData":[TD([[makeQuery(id+"F0.imprint","IMPRINT",EDGE,{"disambiguationData":[TD([[subQ2,-1.0]])],"derivedFrom":subQ1}),1.0]])]});}
            var Q18;
            {var subQ0=sQuery(id+"F0.wireOp",EDGE,"E25");var subQ1=sQuery(id+"F0.wireOp",EDGE,"E3");var subQ2=makeQuery(id+"F0.imprint","INTERSECT",VERTEX,{"derivedFrom":[subQ1,subQ0]});Q18=makeQuery(id+"F0.imprint","IMPRINT",FACE,{"disambiguationData":[TD([[makeQuery(id+"F0.imprint","IMPRINT",EDGE,{"disambiguationData":[TD([[subQ2,-1.0]])],"derivedFrom":subQ1}),1.0]])]});}
            extrude(context, id + "F2", {"entities" : qUnion([Q0, Q1, Q2, Q3, Q4, Q5, Q6, Q7, Q8, Q9, Q10, Q11, Q12, Q13, Q14, Q15, Q16, Q17, Q18]), "operationType" : NewBodyOperationType.ADD, "depth" : 15.24 * mm});
        }
        {
            var Q0;
            {var subQ5=sQuery(id+"F0.wireOp",EDGE,"E3");var subQ7=makeQuery(id+"F0.imprint","INTERSECT",VERTEX,{"derivedFrom":[subQ5,sQuery(id+"F0.wireOp",EDGE,"E23")]});Q0=makeQuery(id+"F0.imprint","IMPRINT",FACE,{"disambiguationData":[TD([[makeQuery(id+"F0.imprint","IMPRINT",EDGE,{"disambiguationData":[TD([[subQ7,-1.0]])],"derivedFrom":subQ5}),1.0]])]});}
            var Q1;
            {var subQ1=sQuery(id+"F0.wireOp",EDGE,"E3");var subQ7=makeQuery(id+"F0.imprint","INTERSECT",VERTEX,{"derivedFrom":[subQ1,sQuery(id+"F0.wireOp",EDGE,"E25")]});Q1=makeQuery(id+"F0.imprint","IMPRINT",FACE,{"disambiguationData":[TD([[makeQuery(id+"F0.imprint","IMPRINT",EDGE,{"disambiguationData":[TD([[subQ7,1.0]])],"derivedFrom":subQ1}),1.0]])]});}
            var Q2;
            {var subQ0=sQuery(id+"F0.wireOp",EDGE,"E14");var subQ1=sQuery(id+"F0.wireOp",EDGE,"E3");var subQ2=makeQuery(id+"F0.imprint","INTERSECT",VERTEX,{"disambiguationData":[OD(1.0)],"derivedFrom":[subQ1,subQ0]});Q2=makeQuery(id+"F0.imprint","IMPRINT",FACE,{"disambiguationData":[TD([[makeQuery(id+"F0.imprint","IMPRINT",EDGE,{"disambiguationData":[TD([[subQ2,-1.0]])],"derivedFrom":subQ1}),1.0]])]});}
            var Q3;
            {var subQ0=sQuery(id+"F0.wireOp",EDGE,"E16");var subQ1=sQuery(id+"F0.wireOp",EDGE,"E3");var subQ2=makeQuery(id+"F0.imprint","INTERSECT",VERTEX,{"disambiguationData":[OD(0.0)],"derivedFrom":[subQ1,subQ0]});Q3=makeQuery(id+"F0.imprint","IMPRINT",FACE,{"disambiguationData":[TD([[makeQuery(id+"F0.imprint","IMPRINT",EDGE,{"disambiguationData":[TD([[subQ2,-1.0]])],"derivedFrom":subQ1}),1.0]])]});}
            var Q4;
            {var subQ0=sQuery(id+"F0.wireOp",EDGE,"E14");var subQ1=sQuery(id+"F0.wireOp",EDGE,"E3");var subQ2=makeQuery(id+"F0.imprint","INTERSECT",VERTEX,{"disambiguationData":[OD(0.0)],"derivedFrom":[subQ1,subQ0]});Q4=makeQuery(id+"F0.imprint","IMPRINT",FACE,{"disambiguationData":[TD([[makeQuery(id+"F0.imprint","IMPRINT",EDGE,{"disambiguationData":[TD([[subQ2,-1.0]])],"derivedFrom":subQ1}),1.0]])]});}
            var Q5;
            {var subQ0=sQuery(id+"F0.wireOp",EDGE,"E17");var subQ1=sQuery(id+"F0.wireOp",EDGE,"E3");var subQ2=makeQuery(id+"F0.imprint","INTERSECT",VERTEX,{"disambiguationData":[OD(0.0)],"derivedFrom":[subQ1,subQ0]});Q5=makeQuery(id+"F0.imprint","IMPRINT",FACE,{"disambiguationData":[TD([[makeQuery(id+"F0.imprint","IMPRINT",EDGE,{"disambiguationData":[TD([[subQ2,-1.0]])],"derivedFrom":subQ1}),1.0]])]});}
            var Q6;
            {var subQ0=sQuery(id+"F0.wireOp",EDGE,"E16");var subQ1=sQuery(id+"F0.wireOp",EDGE,"E3");var subQ2=makeQuery(id+"F0.imprint","INTERSECT",VERTEX,{"disambiguationData":[OD(1.0)],"derivedFrom":[subQ1,subQ0]});Q6=makeQuery(id+"F0.imprint","IMPRINT",FACE,{"disambiguationData":[TD([[makeQuery(id+"F0.imprint","IMPRINT",EDGE,{"disambiguationData":[TD([[subQ2,-1.0]])],"derivedFrom":subQ1}),1.0]])]});}
            var Q7;
            {var subQ0=sQuery(id+"F0.wireOp",EDGE,"E25");var subQ1=sQuery(id+"F0.wireOp",EDGE,"E3");var subQ2=makeQuery(id+"F0.imprint","INTERSECT",VERTEX,{"derivedFrom":[subQ1,subQ0]});Q7=makeQuery(id+"F0.imprint","IMPRINT",FACE,{"disambiguationData":[TD([[makeQuery(id+"F0.imprint","IMPRINT",EDGE,{"disambiguationData":[TD([[subQ2,-1.0]])],"derivedFrom":subQ1}),1.0]])]});}
            extrude(context, id + "F3", {"entities" : qUnion([Q0, Q1, Q2, Q3, Q4, Q5, Q6, Q7]), "operationType" : NewBodyOperationType.REMOVE, "depth" : 10.16 * mm});
        }
        {
            var Q0;
            {var subQ5=sQuery(id+"F0.wireOp",EDGE,"E18");Q0=makeQuery(id+"F0.imprint","IMPRINT",FACE,{"disambiguationData":[TD([[makeQuery(id+"F0.imprint","IMPRINT",EDGE,{"derivedFrom":subQ5}),-1.0]])]});}
            var Q1;
            {var subQ5=sQuery(id+"F0.wireOp",EDGE,"E19");Q1=makeQuery(id+"F0.imprint","IMPRINT",FACE,{"disambiguationData":[TD([[makeQuery(id+"F0.imprint","IMPRINT",EDGE,{"derivedFrom":subQ5}),1.0]])]});}
            var Q2;
            {var subQ0=sQuery(id+"F0.wireOp",EDGE,"E24");Q2=makeQuery(id+"F0.imprint","IMPRINT",FACE,{"disambiguationData":[TD([[makeQuery(id+"F0.imprint","IMPRINT",EDGE,{"derivedFrom":subQ0}),1.0]])]});}
            var Q3;
            {var subQ0=sQuery(id+"F0.wireOp",EDGE,"E25");var subQ1=sQuery(id+"F0.wireOp",EDGE,"E4");var subQ2=makeQuery(id+"F0.imprint","INTERSECT",VERTEX,{"derivedFrom":[subQ1,subQ0]});Q3=makeQuery(id+"F0.imprint","IMPRINT",FACE,{"disambiguationData":[TD([[makeQuery(id+"F0.imprint","IMPRINT",EDGE,{"disambiguationData":[TD([[subQ2,-1.0]])],"derivedFrom":subQ1}),-1.0]])]});}
            var Q4;
            {var subQ0=sQuery(id+"F0.wireOp",EDGE,"E14");var subQ1=sQuery(id+"F0.wireOp",EDGE,"E4");var subQ2=makeQuery(id+"F0.imprint","INTERSECT",VERTEX,{"disambiguationData":[OD(1.0)],"derivedFrom":[subQ1,subQ0]});Q4=makeQuery(id+"F0.imprint","IMPRINT",FACE,{"disambiguationData":[TD([[makeQuery(id+"F0.imprint","IMPRINT",EDGE,{"disambiguationData":[TD([[subQ2,-1.0]])],"derivedFrom":subQ1}),-1.0]])]});}
            extrude(context, id + "F4", {"entities" : qUnion([Q0, Q1, Q2, Q3, Q4]), "operationType" : NewBodyOperationType.ADD, "depth" : 12.7 * mm});
        }
        {
            var Q0;
            Q0=makeQuery(id+"F4.opExtrude","CAP_EDGE",EDGE,{"disambiguationData":[OSD([sQuery(id+"F0.wireOp",EDGE,"E18")])],"isStart":false});
            var Q1;
            Q1=makeQuery(id+"F4.opExtrude","CAP_EDGE",EDGE,{"disambiguationData":[OSD([sQuery(id+"F0.wireOp",EDGE,"E24")])],"isStart":false});
            var Q2;
            Q2=makeQuery(id+"F4.opExtrude","CAP_EDGE",EDGE,{"disambiguationData":[OSD([sQuery(id+"F0.wireOp",EDGE,"E19")])],"isStart":false});
            chamfer(context, id + "F5", {"entities" : qUnion([Q0, Q1, Q2]), "width" : 5.08 * mm, "tangentPropagation" : true});
        }
        {
            var Q0;
            {var subQ0=sQuery(id+"F0.wireOp",EDGE,"E9.MirrorCS");var subQ1=sQuery(id+"F0.wireOp",EDGE,"E5");var subQ2=makeQuery(id+"F0.imprint","INTERSECT",VERTEX,{"derivedFrom":[subQ1,subQ0]});Q0=makeQuery(id+"F0.imprint","IMPRINT",FACE,{"disambiguationData":[TD([[makeQuery(id+"F0.imprint","IMPRINT",EDGE,{"disambiguationData":[TD([[subQ2,1.0]])],"derivedFrom":subQ1}),1.0]])]});}
            extrude(context, id + "F6", {"entities" : qUnion([Q0]), "operationType" : NewBodyOperationType.ADD, "depth" : 7.62 * mm, "hasSecondDirection" : true, "secondDirectionOppositeDirection" : false, "secondDirectionDepth" : 5.08 * mm});
        }
        {
            var Q0;
            {var subQ0=sQuery(id+"F0.wireOp",EDGE,"E6");var subQ1=sQuery(id+"F0.wireOp",EDGE,"E5");var subQ2=makeQuery(id+"F0.imprint","INTERSECT",VERTEX,{"derivedFrom":[subQ1,subQ0]});Q0=makeQuery(id+"F0.imprint","IMPRINT",FACE,{"disambiguationData":[TD([[makeQuery(id+"F0.imprint","IMPRINT",EDGE,{"disambiguationData":[TD([[subQ2,-1.0]])],"derivedFrom":subQ1}),1.0]])]});}
            extrude(context, id + "F7", {"entities" : qUnion([Q0]), "operationType" : NewBodyOperationType.REMOVE, "depth" : 2.54 * mm});
        }
        {
            var Q0;
            {var subQ0=sQuery(id+"F0.wireOp",EDGE,"E29");var subQ1=sQuery(id+"F0.wireOp",EDGE,"E8");var subQ2=makeQuery(id+"F0.imprint","INTERSECT",VERTEX,{"derivedFrom":[subQ1,subQ0]});Q0=makeQuery(id+"F0.imprint","IMPRINT",FACE,{"disambiguationData":[TD([[makeQuery(id+"F0.imprint","IMPRINT",EDGE,{"disambiguationData":[TD([[subQ2,-1.0]])],"derivedFrom":subQ1}),1.0]])]});}
            var Q1;
            {var subQ0=sQuery(id+"F0.wireOp",EDGE,"E29");var subQ1=sQuery(id+"F0.wireOp",EDGE,"E5");var subQ2=makeQuery(id+"F0.imprint","INTERSECT",VERTEX,{"derivedFrom":[subQ1,subQ0]});Q1=makeQuery(id+"F0.imprint","IMPRINT",FACE,{"disambiguationData":[TD([[makeQuery(id+"F0.imprint","IMPRINT",EDGE,{"disambiguationData":[TD([[subQ2,-1.0]])],"derivedFrom":subQ1}),1.0]])]});}
            extrude(context, id + "F8", {"entities" : qUnion([Q0, Q1]), "operationType" : NewBodyOperationType.ADD, "oppositeDirection" : true, "depth" : 5.08 * mm});
        }
        {
            var Q0;
            {var subQ0=sQuery(id+"F0.wireOp",EDGE,"E29");var subQ1=sQuery(id+"F0.wireOp",EDGE,"E5");var subQ2=makeQuery(id+"F0.imprint","INTERSECT",VERTEX,{"derivedFrom":[subQ1,subQ0]});Q0=makeQuery(id+"F0.imprint","IMPRINT",FACE,{"disambiguationData":[TD([[makeQuery(id+"F0.imprint","IMPRINT",EDGE,{"disambiguationData":[TD([[subQ2,-1.0]])],"derivedFrom":subQ1}),1.0]])]});}
            extrude(context, id + "F9", {"entities" : qUnion([Q0]), "operationType" : NewBodyOperationType.REMOVE, "depth" : 2.54 * mm, "hasSecondDirection" : true, "secondDirectionOppositeDirection" : true, "secondDirectionDepth" : 2.54 * mm});
        }
        {
            var Q0;
            Q0=qCreatedBy(makeId("Front.planeOp"),FACE);
            var sketch = newSketch(context, id + "F10", { "sketchPlane" : qUnion([Q0])});
            skLineSegment(sketch, "E35", {"start": v(0, -57.66) * mm, "end": v(0, 68.34) * mm, "construction": true});
            skSolve(sketch);
        }
        {
            var Q0;
            {var subQ0=sQuery(id+"F0.wireOp",EDGE,"E9.MirrorCS");var subQ1=sQuery(id+"F0.wireOp",EDGE,"E0");var subQ2=makeQuery(id+"F0.imprint","INTERSECT",VERTEX,{"derivedFrom":[subQ1,subQ0]});Q0=makeQuery(id+"F0.imprint","IMPRINT",FACE,{"disambiguationData":[TD([[makeQuery(id+"F0.imprint","IMPRINT",EDGE,{"disambiguationData":[TD([[subQ2,1.0]])],"derivedFrom":subQ1}),1.0]])]});}
            var Q1;
            {var subQ0=sQuery(id+"F0.wireOp",EDGE,"E9.MirrorCS");var subQ1=sQuery(id+"F0.wireOp",EDGE,"E0");var subQ2=makeQuery(id+"F0.imprint","INTERSECT",VERTEX,{"derivedFrom":[subQ1,subQ0]});Q1=makeQuery(id+"F0.imprint","IMPRINT",FACE,{"disambiguationData":[TD([[makeQuery(id+"F0.imprint","IMPRINT",EDGE,{"disambiguationData":[TD([[subQ2,-1.0]])],"derivedFrom":subQ1}),1.0]])]});}
            var Q2;
            {var subQ0=sQuery(id+"F0.wireOp",EDGE,"E10.MirrorCS");var subQ1=sQuery(id+"F0.wireOp",EDGE,"E0");var subQ2=makeQuery(id+"F0.imprint","INTERSECT",VERTEX,{"derivedFrom":[subQ1,subQ0]});Q2=makeQuery(id+"F0.imprint","IMPRINT",FACE,{"disambiguationData":[TD([[makeQuery(id+"F0.imprint","IMPRINT",EDGE,{"disambiguationData":[TD([[subQ2,1.0]])],"derivedFrom":subQ1}),1.0]])]});}
            var Q3;
            {var subQ0=sQuery(id+"F0.wireOp",EDGE,"E29");var subQ1=sQuery(id+"F0.wireOp",EDGE,"E0");var subQ2=makeQuery(id+"F0.imprint","INTERSECT",VERTEX,{"derivedFrom":[subQ1,subQ0]});Q3=makeQuery(id+"F0.imprint","IMPRINT",FACE,{"disambiguationData":[TD([[makeQuery(id+"F0.imprint","IMPRINT",EDGE,{"disambiguationData":[TD([[subQ2,-1.0]])],"derivedFrom":subQ1}),1.0]])]});}
            var Q4;
            {var subQ0=sQuery(id+"F0.wireOp",EDGE,"E27");var subQ1=sQuery(id+"F0.wireOp",EDGE,"E0");var subQ2=makeQuery(id+"F0.imprint","INTERSECT",VERTEX,{"derivedFrom":[subQ1,subQ0]});Q4=makeQuery(id+"F0.imprint","IMPRINT",FACE,{"disambiguationData":[TD([[makeQuery(id+"F0.imprint","IMPRINT",EDGE,{"disambiguationData":[TD([[subQ2,-1.0]])],"derivedFrom":subQ1}),1.0]])]});}
            var Q5;
            {var subQ3=sQuery(id+"F0.wireOp",EDGE,"E32");Q5=makeQuery(id+"F0.imprint","IMPRINT",FACE,{"disambiguationData":[TD([[makeQuery(id+"F0.imprint","IMPRINT",EDGE,{"derivedFrom":subQ3}),1.0]])]});}
            var Q6;
            {var subQ0=sQuery(id+"F0.wireOp",EDGE,"E32");Q6=makeQuery(id+"F0.imprint","IMPRINT",FACE,{"disambiguationData":[TD([[makeQuery(id+"F0.imprint","IMPRINT",EDGE,{"derivedFrom":subQ0}),-1.0]])]});}
            var Q7;
            {var subQ0=sQuery(id+"F0.wireOp",EDGE,"E33");Q7=makeQuery(id+"F0.imprint","IMPRINT",FACE,{"disambiguationData":[TD([[makeQuery(id+"F0.imprint","IMPRINT",EDGE,{"derivedFrom":subQ0}),1.0]])]});}
            extrude(context, id + "F11", {"entities" : qUnion([Q0, Q1, Q2, Q3, Q4, Q5, Q6, Q7]), "operationType" : NewBodyOperationType.ADD, "depth" : 10.16 * mm});
        }
    });
